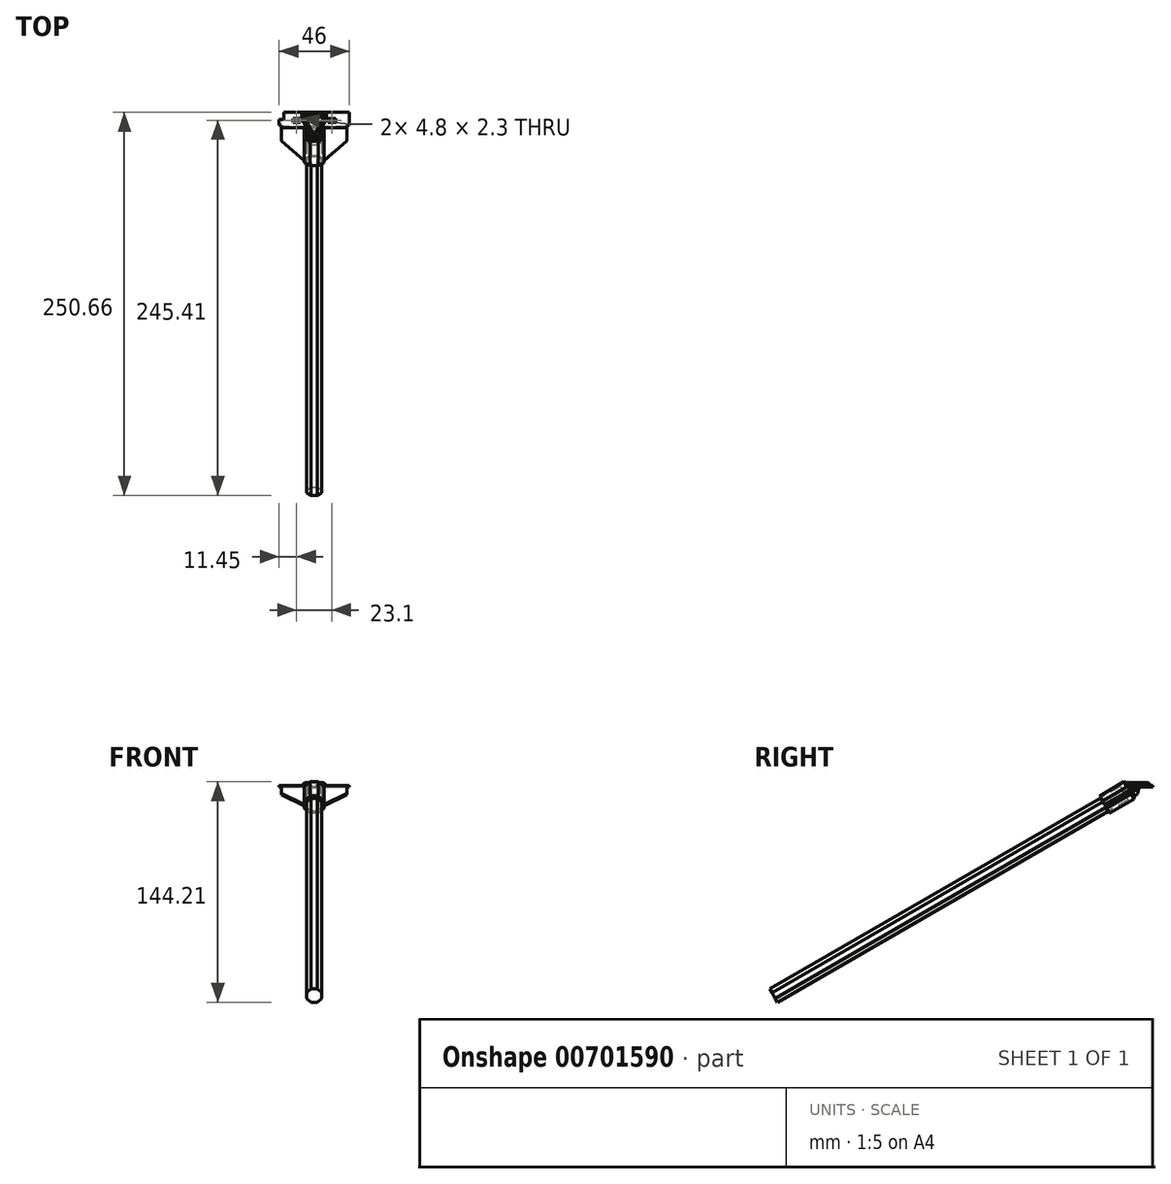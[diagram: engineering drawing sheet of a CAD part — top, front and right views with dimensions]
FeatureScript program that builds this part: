
annotation { "Feature Type Name" : "Feature", "Feature Type Description" : "" }
export const myFeature = defineFeature(function(context is Context, id is Id, definition is map)
    precondition{}
    {
        {
            var Q0;
            Q0=qCreatedBy(makeId("Top.planeOp"),FACE);
            var sketch = newSketch(context, id + "F0", { "sketchPlane" : qUnion([Q0])});
            skLineSegment(sketch, "E0.bottom", {"start": v(-23, 0) * mm, "end": v(23, 0) * mm, "construction": true});
            skLineSegment(sketch, "E0.top", {"start": v(-23, -8.5) * mm, "end": v(23, -8.5) * mm});
            skLineSegment(sketch, "E0.left", {"start": v(-23, 0) * mm, "end": v(-23, -8.5) * mm, "construction": true});
            skLineSegment(sketch, "E0.right", {"start": v(23, 0) * mm, "end": v(23, -8.5) * mm});
            skPoint(sketch, "E1", {"position": v(0, 0) * mm});
            skLineSegment(sketch, "E2", {"start": v(-23, -8.5) * mm, "end": v(-23, -4.5) * mm});
            skLineSegment(sketch, "E3", {"start": v(-23, -4.5) * mm, "end": v(-20, -4.5) * mm});
            skLineSegment(sketch, "E4", {"start": v(-20, -4.5) * mm, "end": v(-20, 0) * mm});
            skLineSegment(sketch, "E5", {"start": v(-20, 0) * mm, "end": v(23, 0) * mm});
            skLineSegment(sketch, "E6", {"start": v(-23, -4.1) * mm, "end": v(23, -4.1) * mm, "construction": true});
            skLineSegment(sketch, "E7", {"start": v(23, -6.4) * mm, "end": v(-23, -6.4) * mm, "construction": true});
            skLineSegment(sketch, "E8.bottom", {"start": v(-13.95, -4.1) * mm, "end": v(-9.15, -4.1) * mm});
            skLineSegment(sketch, "E8.top", {"start": v(-13.95, -6.4) * mm, "end": v(-9.15, -6.4) * mm});
            skLineSegment(sketch, "E8.left", {"start": v(-13.95, -4.1) * mm, "end": v(-13.95, -6.4) * mm});
            skLineSegment(sketch, "E8.right", {"start": v(-9.15, -4.1) * mm, "end": v(-9.15, -6.4) * mm});
            skLineSegment(sketch, "E9.bottom", {"start": v(9.15, -4.1) * mm, "end": v(13.95, -4.1) * mm});
            skLineSegment(sketch, "E9.top", {"start": v(9.15, -6.4) * mm, "end": v(13.95, -6.4) * mm});
            skLineSegment(sketch, "E9.left", {"start": v(9.15, -4.1) * mm, "end": v(9.15, -6.4) * mm});
            skLineSegment(sketch, "E9.right", {"start": v(13.95, -4.1) * mm, "end": v(13.95, -6.4) * mm});
            skLineSegment(sketch, "E10", {"start": v(-21.5, -8.5) * mm, "end": v(-21.5, -10) * mm});
            skLineSegment(sketch, "E11", {"start": v(-21.5, -10) * mm, "end": v(0, -10) * mm});
            skLineSegment(sketch, "E12.MirrorCS", {"start": v(21.5, -10) * mm, "end": v(0, -10) * mm});
            skLineSegment(sketch, "E13.MirrorCS", {"start": v(21.5, -8.5) * mm, "end": v(21.5, -10) * mm});
            skSolve(sketch);
        }
        {
            var Q0;
            {var subQ4=sQuery(id+"F0.wireOp",EDGE,"E0.right");Q0=makeQuery(id+"F0.imprint","IMPRINT",FACE,{"disambiguationData":[TD([[makeQuery(id+"F0.imprint","IMPRINT",EDGE,{"derivedFrom":subQ4}),-1.0]])]});}
            var Q1;
            {var subQ0=sQuery(id+"F0.wireOp",EDGE,"ONbQt4Cq-cTiu-zU10-uyRB-UPFEYYSmvxzo");Q1=makeQuery(id+"F0.imprint","IMPRINT",FACE,{"disambiguationData":[TD([[makeQuery(id+"F0.imprint","IMPRINT",EDGE,{"derivedFrom":subQ0}),1.0]])]});}
            var Q2;
            {var subQ0=sQuery(id+"F0.wireOp",EDGE,"E10");Q2=makeQuery(id+"F0.imprint","IMPRINT",FACE,{"disambiguationData":[TD([[makeQuery(id+"F0.imprint","IMPRINT",EDGE,{"derivedFrom":subQ0}),1.0]])]});}
            extrude(context, id + "F1", {"entities" : qUnion([Q0, Q1, Q2]), "depth" : 1 * mm, "offsetDistance" : 25 * mm});
        }
        {
            var Q0;
            Q0=makeQuery(id+"F1.opExtrude","CAP_EDGE",EDGE,{"disambiguationData":[OSD([sQuery(id+"F0.wireOp",EDGE,"E11"),sQuery(id+"F0.wireOp",EDGE,"E12.MirrorCS")])],"isStart":true});
            chamfer(context, id + "F2", {"entities" : qUnion([Q0]), "chamferType" : ChamferType.OFFSET_ANGLE, "width" : 1 * mm, "oppositeDirection" : false, "angle" : 30 * degree, "tangentPropagation" : true});
        }
        {
            var Q0;
            Q0=makeQuery(id+"F2.opChamfer","BLEND_FACE",FACE,{"disambiguationData":[OSD([sQuery(id+"F0.wireOp",EDGE,"E11"),sQuery(id+"F0.wireOp",EDGE,"E12.MirrorCS")])]});
            extrude(context, id + "F3", {"entities" : qUnion([Q0]), "operationType" : NewBodyOperationType.ADD, "depth" : 25 * mm, "offsetDistance" : 25 * mm});
        }
        {
            var Q0;
            Q0=makeQuery(id+"F1.opExtrude","CAP_FACE",FACE,{"disambiguationData":[OSD([sQuery(id+"F0.wireOp",EDGE,"E0.top"),sQuery(id+"F0.wireOp",EDGE,"E0.right"),sQuery(id+"F0.wireOp",EDGE,"E2"),sQuery(id+"F0.wireOp",EDGE,"E3"),sQuery(id+"F0.wireOp",EDGE,"E4"),sQuery(id+"F0.wireOp",EDGE,"E5"),sQuery(id+"F0.wireOp",EDGE,"E8.bottom"),sQuery(id+"F0.wireOp",EDGE,"E8.top"),sQuery(id+"F0.wireOp",EDGE,"E8.left"),sQuery(id+"F0.wireOp",EDGE,"E8.right"),sQuery(id+"F0.wireOp",EDGE,"E9.bottom"),sQuery(id+"F0.wireOp",EDGE,"E9.top"),sQuery(id+"F0.wireOp",EDGE,"E9.left"),sQuery(id+"F0.wireOp",EDGE,"E9.right"),sQuery(id+"F0.wireOp",EDGE,"E10"),sQuery(id+"F0.wireOp",EDGE,"E11"),sQuery(id+"F0.wireOp",EDGE,"E12.MirrorCS"),sQuery(id+"F0.wireOp",EDGE,"E13.MirrorCS")])],"isStart":false});
            var sketch = newSketch(context, id + "F4", { "sketchPlane" : qUnion([Q0])});
            skLineSegment(sketch, "E14", {"start": v(0, -10) * mm, "end": v(5, -10) * mm});
            skLineSegment(sketch, "E15", {"start": v(5, -10) * mm, "end": v(8.15, -4.1) * mm});
            skLineSegment(sketch, "E16", {"start": v(8.15, -4.1) * mm, "end": v(8.15, -1) * mm});
            skLineSegment(sketch, "E17", {"start": v(8.15, -1) * mm, "end": v(0, -1) * mm});
            skLineSegment(sketch, "E18.MirrorCS", {"start": v(-8.15, -1) * mm, "end": v(0, -1) * mm});
            skLineSegment(sketch, "E19.MirrorCS", {"start": v(-8.15, -4.1) * mm, "end": v(-8.15, -1) * mm});
            skLineSegment(sketch, "E20.MirrorCS", {"start": v(-5, -10) * mm, "end": v(-8.15, -4.1) * mm});
            skLineSegment(sketch, "E21.MirrorCS", {"start": v(0, -10) * mm, "end": v(-5, -10) * mm});
            skSolve(sketch);
        }
        {
            var Q0;
            Q0=makeQuery(id+"F4.imprint","IMPRINT",FACE,{"disambiguationData":[TD([[makeQuery(id+"F4.imprint","IMPRINT",EDGE,{"derivedFrom":sQuery(id+"F4.wireOp",EDGE,"E14")}),1.0]])]});
            extrude(context, id + "F5", {"entities" : qUnion([Q0]), "operationType" : NewBodyOperationType.ADD, "depth" : 2 * mm, "offsetDistance" : 25 * mm});
        }
        {
            var Q0;
            Q0=makeQuery(id+"F5.opExtrude","CAP_EDGE",EDGE,{"disambiguationData":[OSD([sQuery(id+"F4.wireOp",EDGE,"E17"),sQuery(id+"F4.wireOp",EDGE,"E18.MirrorCS")])],"isStart":false});
            var Q1;
            Q1=makeQuery(id+"F5.opExtrude","CAP_EDGE",EDGE,{"disambiguationData":[OSD([sQuery(id+"F4.wireOp",EDGE,"E19.MirrorCS")])],"isStart":false});
            var Q2;
            Q2=makeQuery(id+"F5.opExtrude","CAP_EDGE",EDGE,{"disambiguationData":[OSD([sQuery(id+"F4.wireOp",EDGE,"E16")])],"isStart":false});
            var Q3;
            Q3=makeQuery(id+"F5.opExtrude","CAP_EDGE",EDGE,{"disambiguationData":[OSD([sQuery(id+"F4.wireOp",EDGE,"E15")])],"isStart":false});
            var Q4;
            Q4=makeQuery(id+"F5.opExtrude","CAP_EDGE",EDGE,{"disambiguationData":[OSD([sQuery(id+"F4.wireOp",EDGE,"E20.MirrorCS")])],"isStart":false});
            chamfer(context, id + "F6", {"entities" : qUnion([Q0, Q1, Q2, Q3, Q4]), "width" : 2 * mm, "tangentPropagation" : true});
        }
        {
            var Q0;
            Q0=makeQuery(id+"F3.opExtrude","CAP_FACE",FACE,{"disambiguationData":[OSD([sQuery(id+"F0.wireOp",EDGE,"E11"),sQuery(id+"F0.wireOp",EDGE,"E12.MirrorCS")])],"isStart":false});
            var sketch = newSketch(context, id + "F7", { "sketchPlane" : qUnion([Q0])});
            skCircle(sketch, "E22.cCircle", {"center": v(0, 5.87) * mm, "radius": 5 * mm, "construction": true});
            skLineSegment(sketch, "E22.0", {"start": v(5, 7.94) * mm, "end": v(5, 3.8) * mm});
            skLineSegment(sketch, "E22.1", {"start": v(5, 3.8) * mm, "end": v(2.07, 0.87) * mm});
            skLineSegment(sketch, "E22.2", {"start": v(2.07, 0.87) * mm, "end": v(-2.07, 0.87) * mm});
            skLineSegment(sketch, "E22.3", {"start": v(-2.07, 0.87) * mm, "end": v(-5, 3.8) * mm});
            skLineSegment(sketch, "E22.4", {"start": v(-5, 3.8) * mm, "end": v(-5, 7.94) * mm});
            skLineSegment(sketch, "E22.5", {"start": v(-5, 7.94) * mm, "end": v(-2.07, 10.87) * mm});
            skLineSegment(sketch, "E22.6", {"start": v(-2.07, 10.87) * mm, "end": v(2.07, 10.87) * mm});
            skLineSegment(sketch, "E22.7", {"start": v(2.07, 10.87) * mm, "end": v(5, 7.94) * mm});
            skPoint(sketch, "E22.0.midPoint", {"position": v(5, 5.87) * mm});
            skLineSegment(sketch, "E23.0", {"start": v(2.7, 12.37) * mm, "end": v(6.5, 8.56) * mm});
            skLineSegment(sketch, "E23.1", {"start": v(-2.7, 12.37) * mm, "end": v(2.7, 12.37) * mm});
            skLineSegment(sketch, "E23.2", {"start": v(6.5, 8.56) * mm, "end": v(6.5, 3.17) * mm});
            skLineSegment(sketch, "E23.3", {"start": v(-6.5, 8.56) * mm, "end": v(-2.7, 12.37) * mm});
            skLineSegment(sketch, "E23.4", {"start": v(6.5, 3.17) * mm, "end": v(2.7, -0.63) * mm});
            skLineSegment(sketch, "E23.5", {"start": v(2.7, -0.63) * mm, "end": v(-2.7, -0.63) * mm});
            skLineSegment(sketch, "E23.6", {"start": v(-2.7, -0.63) * mm, "end": v(-6.5, 3.17) * mm});
            skLineSegment(sketch, "E23.7", {"start": v(-6.5, 3.17) * mm, "end": v(-6.5, 8.56) * mm});
            skSolve(sketch);
        }
        {
            var Q0;
            {var subQ24=sQuery(id+"F7.wireOp",EDGE,"E22.1");Q0=makeQuery(id+"F7.imprint","IMPRINT",FACE,{"disambiguationData":[TD([[makeQuery(id+"F7.imprint","IMPRINT",EDGE,{"derivedFrom":subQ24}),-1.0]])]});}
            extrude(context, id + "F8", {"entities" : qUnion([Q0]), "operationType" : NewBodyOperationType.ADD, "oppositeDirection" : true, "depth" : 25 * mm, "offsetDistance" : 25 * mm});
        }
        {
            var Q0;
            {var subQ0=sQuery(id+"F7.wireOp",EDGE,"E22.5");Q0=makeQuery(id+"F7.imprint","IMPRINT",FACE,{"disambiguationData":[TD([[makeQuery(id+"F7.imprint","IMPRINT",EDGE,{"derivedFrom":subQ0}),-1.0]])]});}
            var Q1;
            {var subQ0=sQuery(id+"F4.wireOp",EDGE,"E21.MirrorCS");var subQ1=sQuery(id+"F4.wireOp",EDGE,"E14");var subQ2=sQuery(id+"F4.wireOp",EDGE,"E15");Q1=makeQuery(id+"F6.opChamfer","BLEND_VERTEX",VERTEX,{"blendedFrom":[makeQuery(id+"F5.opExtrude","CAP_EDGE",EDGE,{"disambiguationData":[OSD([subQ2])],"isStart":false}),makeQuery(id+"F5.opExtrude","CAP_FACE",FACE,{"disambiguationData":[OSD([subQ1,subQ2,sQuery(id+"F4.wireOp",EDGE,"E16"),sQuery(id+"F4.wireOp",EDGE,"E17"),sQuery(id+"F4.wireOp",EDGE,"E18.MirrorCS"),sQuery(id+"F4.wireOp",EDGE,"E19.MirrorCS"),sQuery(id+"F4.wireOp",EDGE,"E20.MirrorCS"),subQ0])],"isStart":false}),makeQuery(id+"F5.opExtrude","SWEPT_FACE",FACE,{"disambiguationData":[OSD([subQ1,subQ0])]})],"blendedInto":[makeQuery(id+"F5.opExtrude","CAP_FACE",FACE,{"disambiguationData":[OSD([subQ1,subQ2,sQuery(id+"F4.wireOp",EDGE,"E16"),sQuery(id+"F4.wireOp",EDGE,"E17"),sQuery(id+"F4.wireOp",EDGE,"E18.MirrorCS"),sQuery(id+"F4.wireOp",EDGE,"E19.MirrorCS"),sQuery(id+"F4.wireOp",EDGE,"E20.MirrorCS"),subQ0])],"isStart":false}),makeQuery(id+"F5.opExtrude","SWEPT_FACE",FACE,{"disambiguationData":[OSD([subQ1,subQ0])]})]});}
            extrude(context, id + "F9", {"entities" : qUnion([Q0]), "operationType" : NewBodyOperationType.ADD, "endBound" : BoundingType.UP_TO_VERTEX, "oppositeDirection" : true, "depth" : 25 * mm, "endBoundEntityVertex" : qUnion([Q1]), "offsetDistance" : 25 * mm});
        }
        {
            var Q0;
            Q0=makeQuery(id+"F9.opExtrude","CAP_EDGE",EDGE,{"disambiguationData":[OSD([sQuery(id+"F7.wireOp",EDGE,"E22.6")])],"isStart":false});
            chamfer(context, id + "F10", {"entities" : qUnion([Q0]), "width" : 5 * mm, "tangentPropagation" : true});
        }
        {
            var Q0;
            Q0=makeQuery(id+"F10.opChamfer","BLEND_EDGE",EDGE,{"blendedFrom":[makeQuery(id+"F9.opExtrude","CAP_EDGE",EDGE,{"disambiguationData":[OSD([sQuery(id+"F7.wireOp",EDGE,"E22.6")])],"isStart":false}),makeQuery(id+"F9.opExtrude","SWEPT_FACE",FACE,{"disambiguationData":[OSD([sQuery(id+"F7.wireOp",EDGE,"E22.4")])]})],"blendedInto":[makeQuery(id+"F9.opExtrude","SWEPT_FACE",FACE,{"disambiguationData":[OSD([sQuery(id+"F7.wireOp",EDGE,"E22.4")])]})]});
            var Q1;
            Q1=makeQuery(id+"F10.opChamfer","BLEND_EDGE",EDGE,{"blendedFrom":[makeQuery(id+"F9.opExtrude","CAP_EDGE",EDGE,{"disambiguationData":[OSD([sQuery(id+"F7.wireOp",EDGE,"E22.6")])],"isStart":false}),makeQuery(id+"F9.opExtrude","SWEPT_FACE",FACE,{"disambiguationData":[OSD([sQuery(id+"F7.wireOp",EDGE,"E22.0")])]})],"blendedInto":[makeQuery(id+"F9.opExtrude","SWEPT_FACE",FACE,{"disambiguationData":[OSD([sQuery(id+"F7.wireOp",EDGE,"E22.0")])]})]});
            chamfer(context, id + "F11", {"entities" : qUnion([Q0, Q1]), "width" : 1 * mm, "tangentPropagation" : true});
        }
        {
            var Q0;
            Q0=makeQuery(id+"F8.opExtrude","CAP_EDGE",EDGE,{"disambiguationData":[OSD([sQuery(id+"F7.wireOp",EDGE,"E22.2")])],"isStart":false});
            chamfer(context, id + "F12", {"entities" : qUnion([Q0]), "width" : 3 * mm, "tangentPropagation" : true});
        }
        {
            var Q0;
            Q0=makeQuery(id+"F3.opExtrude","CAP_EDGE",EDGE,{"disambiguationData":[OSD([sQuery(id+"F0.wireOp",EDGE,"E10"),sQuery(id+"F0.wireOp",EDGE,"E11"),sQuery(id+"F0.wireOp",EDGE,"E12.MirrorCS")])],"isStart":false});
            var Q1;
            Q1=makeQuery(id+"F3.opExtrude","CAP_EDGE",EDGE,{"disambiguationData":[OSD([sQuery(id+"F0.wireOp",EDGE,"E11"),sQuery(id+"F0.wireOp",EDGE,"E12.MirrorCS"),sQuery(id+"F0.wireOp",EDGE,"E13.MirrorCS")])],"isStart":false});
            chamfer(context, id + "F13", {"entities" : qUnion([Q0, Q1]), "width" : 15 * mm, "tangentPropagation" : true});
        }
        {
            var Q0;
            {var subQ30=sQuery(id+"F7.wireOp",EDGE,"E22.5");Q0=makeQuery(id+"F7.imprint","IMPRINT",FACE,{"disambiguationData":[TD([[makeQuery(id+"F7.imprint","IMPRINT",EDGE,{"derivedFrom":subQ30}),1.0]])]});}
            var Q1;
            {var subQ26=sQuery(id+"F7.wireOp",EDGE,"E22.1");Q1=makeQuery(id+"F7.imprint","IMPRINT",FACE,{"disambiguationData":[TD([[makeQuery(id+"F7.imprint","IMPRINT",EDGE,{"derivedFrom":subQ26}),1.0]])]});}
            extrude(context, id + "F14", {"entities" : qUnion([Q0, Q1]), "operationType" : NewBodyOperationType.ADD, "oppositeDirection" : true, "depth" : 20 * mm, "offsetDistance" : 25 * mm});
        }
        {
            var Q0;
            Q0=makeQuery(id+"F14.opExtrude","CAP_EDGE",EDGE,{"disambiguationData":[OSD([sQuery(id+"F7.wireOp",EDGE,"E23.0")])],"isStart":false});
            var Q1;
            Q1=makeQuery(id+"F14.opExtrude","CAP_EDGE",EDGE,{"disambiguationData":[OSD([sQuery(id+"F7.wireOp",EDGE,"E23.1")])],"isStart":false});
            var Q2;
            Q2=makeQuery(id+"F14.opExtrude","CAP_EDGE",EDGE,{"disambiguationData":[OSD([sQuery(id+"F7.wireOp",EDGE,"E23.3")])],"isStart":false});
            var Q3;
            {var subQ0=sQuery(id+"F7.wireOp",EDGE,"E23.7");Q3=makeQuery(id+"F14.opExtrude","CAP_EDGE",EDGE,{"disambiguationData":[OSD([subQ0]),TDD([makeQuery(id+"F7.imprint","IMPRINT",EDGE,{"disambiguationData":[TD([[makeQuery(id+"F7.imprint","INTERSECT",VERTEX,{"derivedFrom":[sQuery(id+"F7.wireOp",EDGE,"E23.3"),subQ0]}),1.0]])],"derivedFrom":subQ0})])],"isStart":false});}
            var Q4;
            {var subQ0=sQuery(id+"F7.wireOp",EDGE,"E23.2");Q4=makeQuery(id+"F14.opExtrude","CAP_EDGE",EDGE,{"disambiguationData":[OSD([subQ0]),TDD([makeQuery(id+"F7.imprint","IMPRINT",EDGE,{"disambiguationData":[TD([[makeQuery(id+"F7.imprint","INTERSECT",VERTEX,{"derivedFrom":[sQuery(id+"F7.wireOp",EDGE,"E23.0"),subQ0]}),-1.0]])],"derivedFrom":subQ0})])],"isStart":false});}
            var Q5;
            Q5=makeQuery(id+"F14.opExtrude","CAP_EDGE",EDGE,{"disambiguationData":[OSD([sQuery(id+"F7.wireOp",EDGE,"E23.4")])],"isStart":false});
            var Q6;
            {var subQ0=sQuery(id+"F7.wireOp",EDGE,"E23.2");Q6=makeQuery(id+"F14.opExtrude","CAP_EDGE",EDGE,{"disambiguationData":[OSD([subQ0]),TDD([makeQuery(id+"F7.imprint","IMPRINT",EDGE,{"disambiguationData":[TD([[makeQuery(id+"F7.imprint","INTERSECT",VERTEX,{"derivedFrom":[subQ0,sQuery(id+"F7.wireOp",EDGE,"E23.4")]}),1.0]])],"derivedFrom":subQ0})])],"isStart":false});}
            var Q7;
            Q7=makeQuery(id+"F14.opExtrude","CAP_EDGE",EDGE,{"disambiguationData":[OSD([sQuery(id+"F7.wireOp",EDGE,"E23.5")])],"isStart":false});
            var Q8;
            Q8=makeQuery(id+"F14.opExtrude","CAP_EDGE",EDGE,{"disambiguationData":[OSD([sQuery(id+"F7.wireOp",EDGE,"E23.6")])],"isStart":false});
            var Q9;
            {var subQ0=sQuery(id+"F7.wireOp",EDGE,"E23.7");Q9=makeQuery(id+"F14.opExtrude","CAP_EDGE",EDGE,{"disambiguationData":[OSD([subQ0]),TDD([makeQuery(id+"F7.imprint","IMPRINT",EDGE,{"disambiguationData":[TD([[makeQuery(id+"F7.imprint","INTERSECT",VERTEX,{"derivedFrom":[sQuery(id+"F7.wireOp",EDGE,"E23.6"),subQ0]}),-1.0]])],"derivedFrom":subQ0})])],"isStart":false});}
            chamfer(context, id + "F15", {"entities" : qUnion([Q0, Q1, Q2, Q3, Q4, Q5, Q6, Q7, Q8, Q9]), "width" : 1.5 * mm, "tangentPropagation" : true});
        }
        {
            var Q0;
            {var subQ0=sQuery(id+"F7.wireOp",EDGE,"E22.5");Q0=makeQuery(id+"F7.imprint","IMPRINT",FACE,{"disambiguationData":[TD([[makeQuery(id+"F7.imprint","IMPRINT",EDGE,{"derivedFrom":subQ0}),-1.0]])]});}
            var Q1;
            {var subQ0=sQuery(id+"F7.wireOp",EDGE,"E22.0");var subQ1=sQuery(id+"F0.wireOp",EDGE,"E13.MirrorCS");var subQ2=sQuery(id+"F0.wireOp",EDGE,"E12.MirrorCS");var subQ3=sQuery(id+"F0.wireOp",EDGE,"E11");var subQ4=sQuery(id+"F0.wireOp",EDGE,"E10");var subQ5=sQuery(id+"F0.wireOp",EDGE,"E9.right");var subQ6=sQuery(id+"F0.wireOp",EDGE,"E9.left");var subQ7=sQuery(id+"F0.wireOp",EDGE,"E9.top");var subQ8=sQuery(id+"F0.wireOp",EDGE,"E9.bottom");var subQ9=sQuery(id+"F0.wireOp",EDGE,"E8.right");var subQ10=sQuery(id+"F0.wireOp",EDGE,"E8.left");var subQ11=sQuery(id+"F0.wireOp",EDGE,"E8.top");var subQ12=sQuery(id+"F0.wireOp",EDGE,"E8.bottom");var subQ13=sQuery(id+"F0.wireOp",EDGE,"E5");var subQ14=sQuery(id+"F0.wireOp",EDGE,"E4");var subQ15=sQuery(id+"F0.wireOp",EDGE,"E3");var subQ16=sQuery(id+"F0.wireOp",EDGE,"E2");var subQ17=sQuery(id+"F0.wireOp",EDGE,"E0.right");var subQ18=sQuery(id+"F0.wireOp",EDGE,"E0.top");var subQ19=makeQuery(id+"F1.opExtrude","CAP_EDGE",EDGE,{"disambiguationData":[OSD([subQ3,subQ2])],"isStart":true});var subQ20=makeQuery(id+"F3.opExtrude","CAP_EDGE",EDGE,{"disambiguationData":[OSD([subQ18,subQ17,subQ16,subQ15,subQ14,subQ13,subQ12,subQ11,subQ10,subQ9,subQ8,subQ7,subQ6,subQ5,subQ4,subQ3,subQ2,subQ1]),TDD([makeQuery(id+"F2.opChamfer","BLEND_EDGE",EDGE,{"blendedFrom":[subQ19,makeQuery(id+"F1.opExtrude","CAP_FACE",FACE,{"disambiguationData":[OSD([subQ18,subQ17,subQ16,subQ15,subQ14,subQ13,subQ12,subQ11,subQ10,subQ9,subQ8,subQ7,subQ6,subQ5,subQ4,subQ3,subQ2,subQ1])],"isStart":false})],"blendedInto":[makeQuery(id+"F1.opExtrude","CAP_FACE",FACE,{"disambiguationData":[OSD([subQ18,subQ17,subQ16,subQ15,subQ14,subQ13,subQ12,subQ11,subQ10,subQ9,subQ8,subQ7,subQ6,subQ5,subQ4,subQ3,subQ2,subQ1])],"isStart":false})]})])],"isStart":false});var subQ21=makeQuery(id+"F7.imprint","INTERSECT",VERTEX,{"derivedFrom":[subQ20,subQ0]});Q1=makeQuery(id+"F7.imprint","IMPRINT",FACE,{"disambiguationData":[TD([[makeQuery(id+"F7.imprint","IMPRINT",EDGE,{"disambiguationData":[TD([[subQ21,-1.0]])],"derivedFrom":subQ0}),-1.0]])]});}
            var Q2;
            {var subQ1=sQuery(id+"F7.wireOp",EDGE,"E22.1");Q2=makeQuery(id+"F7.imprint","IMPRINT",FACE,{"disambiguationData":[TD([[makeQuery(id+"F7.imprint","IMPRINT",EDGE,{"derivedFrom":subQ1}),-1.0]])]});}
            extrude(context, id + "F16", {"entities" : qUnion([Q0, Q1, Q2]), "operationType" : NewBodyOperationType.REMOVE, "oppositeDirection" : true, "depth" : 15 * mm, "offsetDistance" : 25 * mm});
        }
        {
            var Q0;
            {var subQ0=sQuery(id+"F7.wireOp",EDGE,"E22.0");var subQ1=sQuery(id+"F0.wireOp",EDGE,"E13.MirrorCS");var subQ2=sQuery(id+"F0.wireOp",EDGE,"E12.MirrorCS");var subQ3=sQuery(id+"F0.wireOp",EDGE,"E11");var subQ4=sQuery(id+"F0.wireOp",EDGE,"E10");var subQ5=sQuery(id+"F0.wireOp",EDGE,"E9.right");var subQ6=sQuery(id+"F0.wireOp",EDGE,"E9.left");var subQ7=sQuery(id+"F0.wireOp",EDGE,"E9.top");var subQ8=sQuery(id+"F0.wireOp",EDGE,"E9.bottom");var subQ9=sQuery(id+"F0.wireOp",EDGE,"E8.right");var subQ10=sQuery(id+"F0.wireOp",EDGE,"E8.left");var subQ11=sQuery(id+"F0.wireOp",EDGE,"E8.top");var subQ12=sQuery(id+"F0.wireOp",EDGE,"E8.bottom");var subQ13=sQuery(id+"F0.wireOp",EDGE,"E5");var subQ14=sQuery(id+"F0.wireOp",EDGE,"E4");var subQ15=sQuery(id+"F0.wireOp",EDGE,"E3");var subQ16=sQuery(id+"F0.wireOp",EDGE,"E2");var subQ17=sQuery(id+"F0.wireOp",EDGE,"E0.right");var subQ18=sQuery(id+"F0.wireOp",EDGE,"E0.top");var subQ19=makeQuery(id+"F1.opExtrude","CAP_EDGE",EDGE,{"disambiguationData":[OSD([subQ3,subQ2])],"isStart":true});var subQ20=makeQuery(id+"F3.opExtrude","CAP_EDGE",EDGE,{"disambiguationData":[OSD([subQ18,subQ17,subQ16,subQ15,subQ14,subQ13,subQ12,subQ11,subQ10,subQ9,subQ8,subQ7,subQ6,subQ5,subQ4,subQ3,subQ2,subQ1]),TDD([makeQuery(id+"F2.opChamfer","BLEND_EDGE",EDGE,{"blendedFrom":[subQ19,makeQuery(id+"F1.opExtrude","CAP_FACE",FACE,{"disambiguationData":[OSD([subQ18,subQ17,subQ16,subQ15,subQ14,subQ13,subQ12,subQ11,subQ10,subQ9,subQ8,subQ7,subQ6,subQ5,subQ4,subQ3,subQ2,subQ1])],"isStart":false})],"blendedInto":[makeQuery(id+"F1.opExtrude","CAP_FACE",FACE,{"disambiguationData":[OSD([subQ18,subQ17,subQ16,subQ15,subQ14,subQ13,subQ12,subQ11,subQ10,subQ9,subQ8,subQ7,subQ6,subQ5,subQ4,subQ3,subQ2,subQ1])],"isStart":false})]})])],"isStart":false});var subQ21=makeQuery(id+"F7.imprint","INTERSECT",VERTEX,{"derivedFrom":[subQ20,subQ0]});Q0=makeQuery(id+"F7.imprint","IMPRINT",FACE,{"disambiguationData":[TD([[makeQuery(id+"F7.imprint","IMPRINT",EDGE,{"disambiguationData":[TD([[subQ21,-1.0]])],"derivedFrom":subQ0}),-1.0]])]});}
            var Q1;
            {var subQ0=sQuery(id+"F7.wireOp",EDGE,"E22.5");Q1=makeQuery(id+"F7.imprint","IMPRINT",FACE,{"disambiguationData":[TD([[makeQuery(id+"F7.imprint","IMPRINT",EDGE,{"derivedFrom":subQ0}),-1.0]])]});}
            var Q2;
            {var subQ1=sQuery(id+"F7.wireOp",EDGE,"E22.1");Q2=makeQuery(id+"F7.imprint","IMPRINT",FACE,{"disambiguationData":[TD([[makeQuery(id+"F7.imprint","IMPRINT",EDGE,{"derivedFrom":subQ1}),-1.0]])]});}
            extrude(context, id + "F17", {"entities" : qUnion([Q0, Q1, Q2]), "depth" : 250 * mm, "offsetDistance" : 25 * mm});
        }
        {
            var Q0;
            {var subQ0=sQuery(id+"F7.wireOp",EDGE,"E23.2");var subQ1=sQuery(id+"F0.wireOp",EDGE,"E13.MirrorCS");var subQ2=sQuery(id+"F0.wireOp",EDGE,"E12.MirrorCS");var subQ3=sQuery(id+"F0.wireOp",EDGE,"E11");var subQ4=sQuery(id+"F0.wireOp",EDGE,"E10");var subQ5=sQuery(id+"F0.wireOp",EDGE,"E9.right");var subQ6=sQuery(id+"F0.wireOp",EDGE,"E9.left");var subQ7=sQuery(id+"F0.wireOp",EDGE,"E9.top");var subQ8=sQuery(id+"F0.wireOp",EDGE,"E9.bottom");var subQ9=sQuery(id+"F0.wireOp",EDGE,"E8.right");var subQ10=sQuery(id+"F0.wireOp",EDGE,"E8.left");var subQ11=sQuery(id+"F0.wireOp",EDGE,"E8.top");var subQ12=sQuery(id+"F0.wireOp",EDGE,"E8.bottom");var subQ13=sQuery(id+"F0.wireOp",EDGE,"E5");var subQ14=sQuery(id+"F0.wireOp",EDGE,"E4");var subQ15=sQuery(id+"F0.wireOp",EDGE,"E3");var subQ16=sQuery(id+"F0.wireOp",EDGE,"E2");var subQ17=sQuery(id+"F0.wireOp",EDGE,"E0.right");var subQ18=sQuery(id+"F0.wireOp",EDGE,"E0.top");Q0=makeQuery(id+"F14.opExtrude","SWEPT_EDGE",EDGE,{"disambiguationData":[OSD([subQ18,subQ17,subQ16,subQ15,subQ14,subQ13,subQ12,subQ11,subQ10,subQ9,subQ8,subQ7,subQ6,subQ5,subQ4,subQ3,subQ2,subQ1,subQ0]),TDD([makeQuery(id+"F7.imprint","INTERSECT",VERTEX,{"derivedFrom":[makeQuery(id+"F3.opExtrude","CAP_EDGE",EDGE,{"disambiguationData":[OSD([subQ18,subQ17,subQ16,subQ15,subQ14,subQ13,subQ12,subQ11,subQ10,subQ9,subQ8,subQ7,subQ6,subQ5,subQ4,subQ3,subQ2,subQ1]),TDD([makeQuery(id+"F2.opChamfer","BLEND_EDGE",EDGE,{"blendedFrom":[makeQuery(id+"F1.opExtrude","CAP_EDGE",EDGE,{"disambiguationData":[OSD([subQ3,subQ2])],"isStart":true}),makeQuery(id+"F1.opExtrude","CAP_FACE",FACE,{"disambiguationData":[OSD([subQ18,subQ17,subQ16,subQ15,subQ14,subQ13,subQ12,subQ11,subQ10,subQ9,subQ8,subQ7,subQ6,subQ5,subQ4,subQ3,subQ2,subQ1])],"isStart":false})],"blendedInto":[makeQuery(id+"F1.opExtrude","CAP_FACE",FACE,{"disambiguationData":[OSD([subQ18,subQ17,subQ16,subQ15,subQ14,subQ13,subQ12,subQ11,subQ10,subQ9,subQ8,subQ7,subQ6,subQ5,subQ4,subQ3,subQ2,subQ1])],"isStart":false})]})])],"isStart":false}),subQ0]})])]});}
            var Q1;
            {var subQ0=sQuery(id+"F0.wireOp",EDGE,"E13.MirrorCS");var subQ1=sQuery(id+"F0.wireOp",EDGE,"E12.MirrorCS");var subQ2=sQuery(id+"F0.wireOp",EDGE,"E11");var subQ3=sQuery(id+"F0.wireOp",EDGE,"E10");var subQ4=sQuery(id+"F0.wireOp",EDGE,"E9.right");var subQ5=sQuery(id+"F0.wireOp",EDGE,"E9.left");var subQ6=sQuery(id+"F0.wireOp",EDGE,"E9.top");var subQ7=sQuery(id+"F0.wireOp",EDGE,"E9.bottom");var subQ8=sQuery(id+"F0.wireOp",EDGE,"E8.right");var subQ9=sQuery(id+"F0.wireOp",EDGE,"E8.left");var subQ10=sQuery(id+"F0.wireOp",EDGE,"E8.top");var subQ11=sQuery(id+"F0.wireOp",EDGE,"E8.bottom");var subQ12=sQuery(id+"F0.wireOp",EDGE,"E5");var subQ13=sQuery(id+"F0.wireOp",EDGE,"E4");var subQ14=sQuery(id+"F0.wireOp",EDGE,"E3");var subQ15=sQuery(id+"F0.wireOp",EDGE,"E2");var subQ16=sQuery(id+"F0.wireOp",EDGE,"E0.right");var subQ17=sQuery(id+"F0.wireOp",EDGE,"E0.top");var subQ18=makeQuery(id+"F1.opExtrude","CAP_FACE",FACE,{"disambiguationData":[OSD([subQ17,subQ16,subQ15,subQ14,subQ13,subQ12,subQ11,subQ10,subQ9,subQ8,subQ7,subQ6,subQ5,subQ4,subQ3,subQ2,subQ1,subQ0])],"isStart":false});var subQ21=makeQuery(id+"F2.opChamfer","BLEND_EDGE",EDGE,{"blendedFrom":[makeQuery(id+"F1.opExtrude","CAP_EDGE",EDGE,{"disambiguationData":[OSD([subQ2,subQ1])],"isStart":true}),subQ18],"blendedInto":[subQ18]});var subQ22=sQuery(id+"F7.wireOp",EDGE,"E23.2");Q1=makeQuery(id+"F15.opChamfer","BLEND_EDGE",EDGE,{"blendedFrom":[makeQuery(id+"F14.opExtrude","CAP_EDGE",EDGE,{"disambiguationData":[OSD([subQ22]),TDD([makeQuery(id+"F7.imprint","IMPRINT",EDGE,{"disambiguationData":[TD([[makeQuery(id+"F7.imprint","INTERSECT",VERTEX,{"derivedFrom":[sQuery(id+"F7.wireOp",EDGE,"E23.0"),subQ22]}),-1.0]])],"derivedFrom":subQ22})])],"isStart":false}),makeQuery(id+"F9.boolean.opBoolean","SPLIT",FACE,{"disambiguationData":[TD([makeQuery(id+"F1.opExtrude","SWEPT_FACE",FACE,{"disambiguationData":[OSD([subQ0])]})])],"derivedFrom":makeQuery(id+"F3.opExtrude","SWEPT_FACE",FACE,{"disambiguationData":[OSD([subQ17,subQ16,subQ15,subQ14,subQ13,subQ12,subQ11,subQ10,subQ9,subQ8,subQ7,subQ6,subQ5,subQ4,subQ3,subQ2,subQ1,subQ0]),TDD([subQ21])]})})],"blendedInto":[makeQuery(id+"F9.boolean.opBoolean","SPLIT",FACE,{"disambiguationData":[TD([makeQuery(id+"F1.opExtrude","SWEPT_FACE",FACE,{"disambiguationData":[OSD([subQ0])]})])],"derivedFrom":makeQuery(id+"F3.opExtrude","SWEPT_FACE",FACE,{"disambiguationData":[OSD([subQ17,subQ16,subQ15,subQ14,subQ13,subQ12,subQ11,subQ10,subQ9,subQ8,subQ7,subQ6,subQ5,subQ4,subQ3,subQ2,subQ1,subQ0]),TDD([subQ21])]})})]});}
            var Q2;
            {var subQ0=sQuery(id+"F0.wireOp",EDGE,"E12.MirrorCS");var subQ1=sQuery(id+"F0.wireOp",EDGE,"E11");var subQ2=sQuery(id+"F0.wireOp",EDGE,"E10");var subQ3=sQuery(id+"F0.wireOp",EDGE,"E13.MirrorCS");var subQ4=sQuery(id+"F0.wireOp",EDGE,"E9.right");var subQ5=sQuery(id+"F0.wireOp",EDGE,"E9.left");var subQ6=sQuery(id+"F0.wireOp",EDGE,"E9.top");var subQ7=sQuery(id+"F0.wireOp",EDGE,"E9.bottom");var subQ8=sQuery(id+"F0.wireOp",EDGE,"E8.right");var subQ9=sQuery(id+"F0.wireOp",EDGE,"E8.left");var subQ10=sQuery(id+"F0.wireOp",EDGE,"E8.top");var subQ11=sQuery(id+"F0.wireOp",EDGE,"E8.bottom");var subQ12=sQuery(id+"F0.wireOp",EDGE,"E5");var subQ13=sQuery(id+"F0.wireOp",EDGE,"E4");var subQ14=sQuery(id+"F0.wireOp",EDGE,"E3");var subQ15=sQuery(id+"F0.wireOp",EDGE,"E2");var subQ16=sQuery(id+"F0.wireOp",EDGE,"E0.right");var subQ17=sQuery(id+"F0.wireOp",EDGE,"E0.top");var subQ18=makeQuery(id+"F1.opExtrude","CAP_FACE",FACE,{"disambiguationData":[OSD([subQ17,subQ16,subQ15,subQ14,subQ13,subQ12,subQ11,subQ10,subQ9,subQ8,subQ7,subQ6,subQ5,subQ4,subQ2,subQ1,subQ0,subQ3])],"isStart":false});var subQ21=makeQuery(id+"F2.opChamfer","BLEND_EDGE",EDGE,{"blendedFrom":[makeQuery(id+"F1.opExtrude","CAP_EDGE",EDGE,{"disambiguationData":[OSD([subQ1,subQ0])],"isStart":true}),subQ18],"blendedInto":[subQ18]});var subQ22=sQuery(id+"F7.wireOp",EDGE,"E23.7");Q2=makeQuery(id+"F15.opChamfer","BLEND_EDGE",EDGE,{"blendedFrom":[makeQuery(id+"F14.opExtrude","CAP_EDGE",EDGE,{"disambiguationData":[OSD([subQ22]),TDD([makeQuery(id+"F7.imprint","IMPRINT",EDGE,{"disambiguationData":[TD([[makeQuery(id+"F7.imprint","INTERSECT",VERTEX,{"derivedFrom":[sQuery(id+"F7.wireOp",EDGE,"E23.3"),subQ22]}),1.0]])],"derivedFrom":subQ22})])],"isStart":false}),makeQuery(id+"F9.boolean.opBoolean","SPLIT",FACE,{"disambiguationData":[TD([makeQuery(id+"F1.opExtrude","SWEPT_FACE",FACE,{"disambiguationData":[OSD([subQ2])]})])],"derivedFrom":makeQuery(id+"F3.opExtrude","SWEPT_FACE",FACE,{"disambiguationData":[OSD([subQ17,subQ16,subQ15,subQ14,subQ13,subQ12,subQ11,subQ10,subQ9,subQ8,subQ7,subQ6,subQ5,subQ4,subQ2,subQ1,subQ0,subQ3]),TDD([subQ21])]})})],"blendedInto":[makeQuery(id+"F9.boolean.opBoolean","SPLIT",FACE,{"disambiguationData":[TD([makeQuery(id+"F1.opExtrude","SWEPT_FACE",FACE,{"disambiguationData":[OSD([subQ2])]})])],"derivedFrom":makeQuery(id+"F3.opExtrude","SWEPT_FACE",FACE,{"disambiguationData":[OSD([subQ17,subQ16,subQ15,subQ14,subQ13,subQ12,subQ11,subQ10,subQ9,subQ8,subQ7,subQ6,subQ5,subQ4,subQ2,subQ1,subQ0,subQ3]),TDD([subQ21])]})})]});}
            var Q3;
            {var subQ0=sQuery(id+"F7.wireOp",EDGE,"E23.7");var subQ1=sQuery(id+"F0.wireOp",EDGE,"E13.MirrorCS");var subQ2=sQuery(id+"F0.wireOp",EDGE,"E12.MirrorCS");var subQ3=sQuery(id+"F0.wireOp",EDGE,"E11");var subQ4=sQuery(id+"F0.wireOp",EDGE,"E10");var subQ5=sQuery(id+"F0.wireOp",EDGE,"E9.right");var subQ6=sQuery(id+"F0.wireOp",EDGE,"E9.left");var subQ7=sQuery(id+"F0.wireOp",EDGE,"E9.top");var subQ8=sQuery(id+"F0.wireOp",EDGE,"E9.bottom");var subQ9=sQuery(id+"F0.wireOp",EDGE,"E8.right");var subQ10=sQuery(id+"F0.wireOp",EDGE,"E8.left");var subQ11=sQuery(id+"F0.wireOp",EDGE,"E8.top");var subQ12=sQuery(id+"F0.wireOp",EDGE,"E8.bottom");var subQ13=sQuery(id+"F0.wireOp",EDGE,"E5");var subQ14=sQuery(id+"F0.wireOp",EDGE,"E4");var subQ15=sQuery(id+"F0.wireOp",EDGE,"E3");var subQ16=sQuery(id+"F0.wireOp",EDGE,"E2");var subQ17=sQuery(id+"F0.wireOp",EDGE,"E0.right");var subQ18=sQuery(id+"F0.wireOp",EDGE,"E0.top");Q3=makeQuery(id+"F14.opExtrude","SWEPT_EDGE",EDGE,{"disambiguationData":[OSD([subQ18,subQ17,subQ16,subQ15,subQ14,subQ13,subQ12,subQ11,subQ10,subQ9,subQ8,subQ7,subQ6,subQ5,subQ4,subQ3,subQ2,subQ1,subQ0]),TDD([makeQuery(id+"F7.imprint","INTERSECT",VERTEX,{"derivedFrom":[makeQuery(id+"F3.opExtrude","CAP_EDGE",EDGE,{"disambiguationData":[OSD([subQ18,subQ17,subQ16,subQ15,subQ14,subQ13,subQ12,subQ11,subQ10,subQ9,subQ8,subQ7,subQ6,subQ5,subQ4,subQ3,subQ2,subQ1]),TDD([makeQuery(id+"F2.opChamfer","BLEND_EDGE",EDGE,{"blendedFrom":[makeQuery(id+"F1.opExtrude","CAP_EDGE",EDGE,{"disambiguationData":[OSD([subQ3,subQ2])],"isStart":true}),makeQuery(id+"F1.opExtrude","CAP_FACE",FACE,{"disambiguationData":[OSD([subQ18,subQ17,subQ16,subQ15,subQ14,subQ13,subQ12,subQ11,subQ10,subQ9,subQ8,subQ7,subQ6,subQ5,subQ4,subQ3,subQ2,subQ1])],"isStart":false})],"blendedInto":[makeQuery(id+"F1.opExtrude","CAP_FACE",FACE,{"disambiguationData":[OSD([subQ18,subQ17,subQ16,subQ15,subQ14,subQ13,subQ12,subQ11,subQ10,subQ9,subQ8,subQ7,subQ6,subQ5,subQ4,subQ3,subQ2,subQ1])],"isStart":false})]})])],"isStart":false}),subQ0]})])]});}
            fillet(context, id + "F18", {"entities" : qUnion([Q0, Q1, Q2, Q3]), "radius" : 5 * mm, "tangentPropagation" : true, "allowEdgeOverflow" : false});
        }
    });
